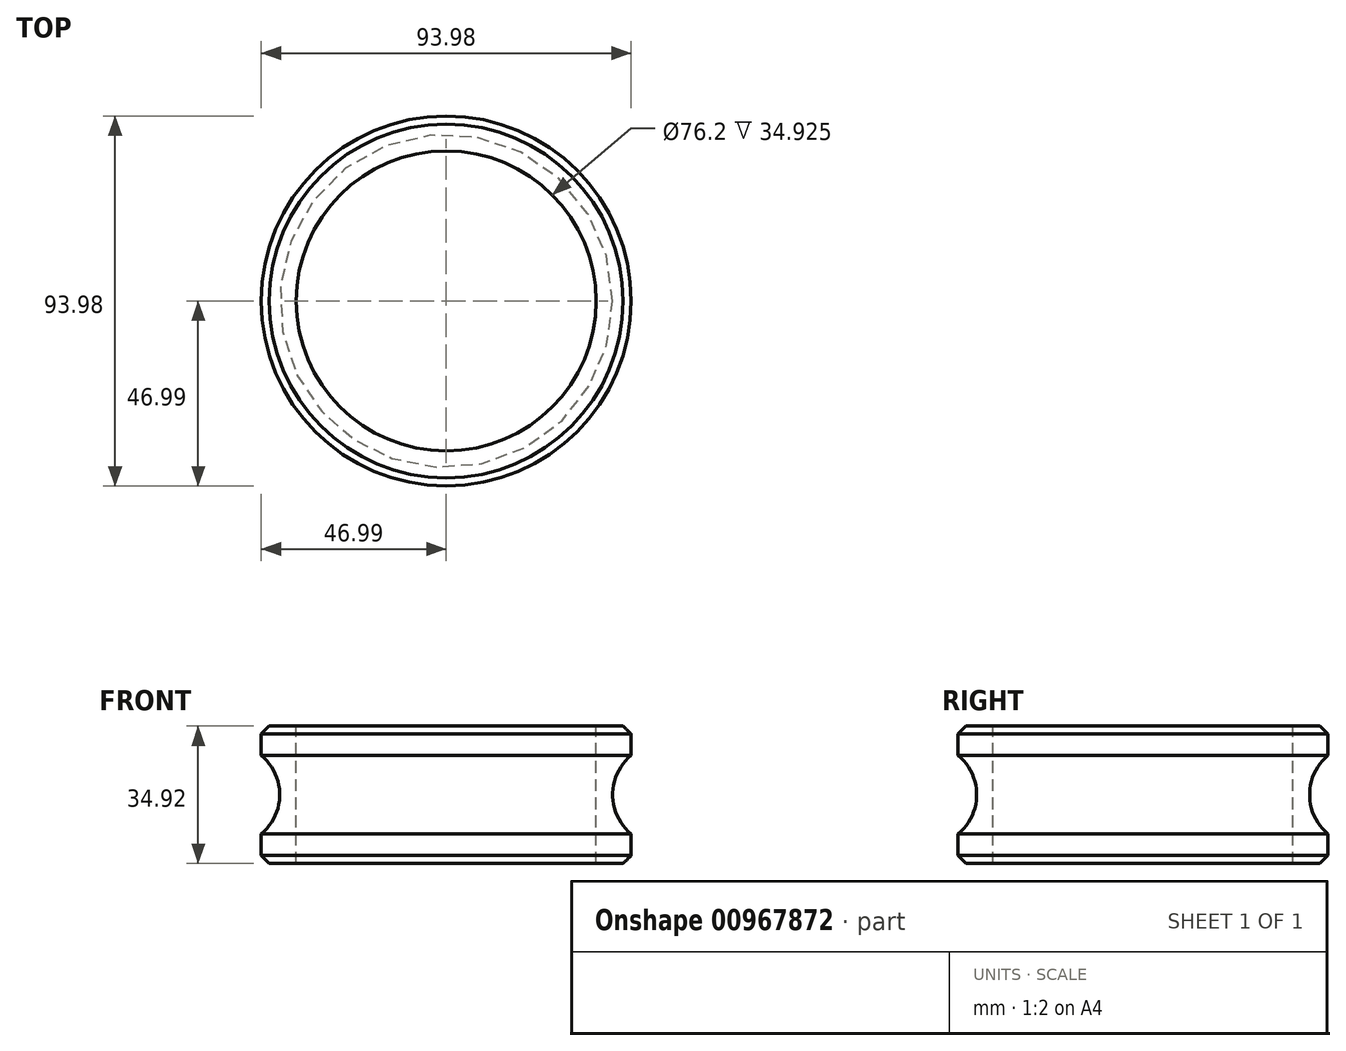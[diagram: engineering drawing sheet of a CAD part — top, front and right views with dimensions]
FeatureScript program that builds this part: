
annotation { "Feature Type Name" : "Feature", "Feature Type Description" : "" }
export const myFeature = defineFeature(function(context is Context, id is Id, definition is map)
    precondition{}
    {
        {
            var Q0;
            Q0=qCreatedBy(makeId("Front.planeOp"),FACE);
            var sketch = newSketch(context, id + "F0", { "sketchPlane" : qUnion([Q0])});
            skLineSegment(sketch, "E0", {"start": v(38.1, 17.46) * mm, "end": v(38.1, -17.46) * mm});
            skCircle(sketch, "E1", {"center": v(55.25, 0) * mm, "radius": 12.7 * mm, "construction": true});
            skLineSegment(sketch, "E2", {"start": v(38.1, 17.46) * mm, "end": v(47, 17.46) * mm});
            skLineSegment(sketch, "E3", {"start": v(38.1, -17.46) * mm, "end": v(47, -17.46) * mm});
            skArc(sketch, "E4", {"start": v(47, 9.98) * mm, "mid": v(42.3, 0) * mm, "end": v(47, -9.98) * mm});
            skLineSegment(sketch, "E5", {"start": v(47, 17.46) * mm, "end": v(47, 9.98) * mm});
            skLineSegment(sketch, "E6", {"start": v(47, -17.46) * mm, "end": v(47, -9.98) * mm});
            skSolve(sketch);
        }
        {
            var Q0;
            Q0=qCreatedBy(makeId("Front.planeOp"),FACE);
            var sketch = newSketch(context, id + "F1", { "sketchPlane" : qUnion([Q0])});
            skLineSegment(sketch, "E7", {"start": v(0, 33.66) * mm, "end": v(0, -32.44) * mm});
            skSolve(sketch);
        }
        {
            var Q0;
            Q0 = qSketchRegion(id + "F0", true);
            var Q1;
            Q1=sQuery(id+"F1.wireOp",EDGE,"E7");
            revolve(context, id + "F2", {"surfaceOperationType" : NewSurfaceOperationType.NEW, "entities" : qUnion([Q0]), "axis" : qUnion([Q1]), "revolveType" : RevolveType.FULL});
        }
        {
            var Q0;
            Q0=makeQuery(id+"F2.opRevolve","SWEPT_EDGE",EDGE,{"disambiguationData":[OSD([sQuery(id+"F0.wireOp",EDGE,"E2"),sQuery(id+"F0.wireOp",EDGE,"E5")])]});
            var Q1;
            Q1=makeQuery(id+"F2.opRevolve","SWEPT_EDGE",EDGE,{"disambiguationData":[OSD([sQuery(id+"F0.wireOp",EDGE,"E3"),sQuery(id+"F0.wireOp",EDGE,"E6")])]});
            chamfer(context, id + "F3", {"entities" : qUnion([Q0, Q1]), "width" : 2.03 * mm, "tangentPropagation" : true});
        }
    });
